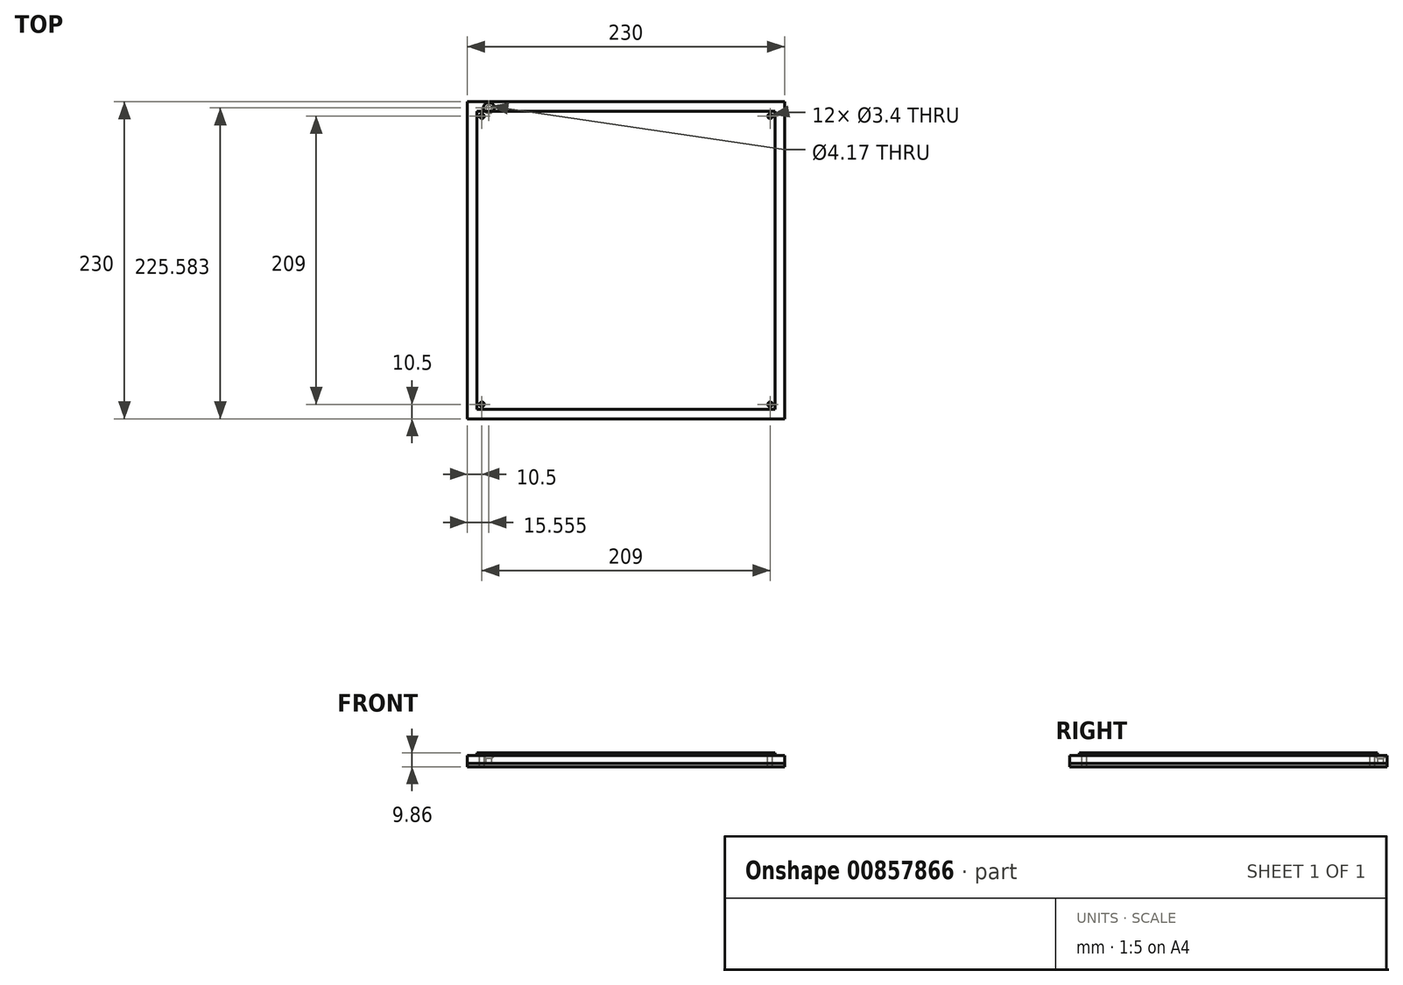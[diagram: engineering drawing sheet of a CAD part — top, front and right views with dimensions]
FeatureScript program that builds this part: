
annotation { "Feature Type Name" : "Feature", "Feature Type Description" : "" }
export const myFeature = defineFeature(function(context is Context, id is Id, definition is map)
    precondition{}
    {
        {
            var Q0;
            Q0=qCreatedBy(makeId("Top.planeOp"),FACE);
            var sketch = newSketch(context, id + "F0", { "sketchPlane" : qUnion([Q0])});
            skLineSegment(sketch, "E0.bottom", {"start": v(108, -108) * mm, "end": v(-108, -108) * mm});
            skLineSegment(sketch, "E0.top", {"start": v(108, 108) * mm, "end": v(-108, 108) * mm});
            skLineSegment(sketch, "E0.left", {"start": v(108, -108) * mm, "end": v(108, 108) * mm});
            skLineSegment(sketch, "E0.right", {"start": v(-108, -108) * mm, "end": v(-108, 108) * mm});
            skPoint(sketch, "E0.middle", {"position": v(0, 0) * mm});
            skCircle(sketch, "E1", {"center": v(-104.5, 104.5) * mm, "radius": 1.7 * mm});
            skCircle(sketch, "E2", {"center": v(104.5, 104.5) * mm, "radius": 1.7 * mm});
            skCircle(sketch, "E3", {"center": v(-104.5, -104.5) * mm, "radius": 1.7 * mm});
            skCircle(sketch, "E4", {"center": v(104.5, -104.5) * mm, "radius": 1.7 * mm});
            skSolve(sketch);
        }
        {
            var Q0;
            Q0 = qSketchRegion(id + "F0", true);
            extrude(context, id + "F1", {"entities" : qUnion([Q0]), "depth" : 1.86 * mm, "offsetDistance" : 25 * mm});
        }
        {
            var Q0;
            Q0=qCreatedBy(makeId("Top.planeOp"),FACE);
            var sketch = newSketch(context, id + "F2", { "sketchPlane" : qUnion([Q0])});
            skLineSegment(sketch, "E5.bottom", {"start": v(115, -115) * mm, "end": v(-115, -115) * mm});
            skLineSegment(sketch, "E5.top", {"start": v(115, 115) * mm, "end": v(-115, 115) * mm});
            skLineSegment(sketch, "E5.left", {"start": v(115, -115) * mm, "end": v(115, 115) * mm});
            skLineSegment(sketch, "E5.right", {"start": v(-115, -115) * mm, "end": v(-115, 115) * mm});
            skPoint(sketch, "E5.middle", {"position": v(0, 0) * mm});
            skCircle(sketch, "E6.0", {"center": v(-104.5, 104.5) * mm, "radius": 1.7 * mm});
            skCircle(sketch, "E7.0", {"center": v(104.5, 104.5) * mm, "radius": 1.7 * mm});
            skCircle(sketch, "E8.0", {"center": v(104.5, -104.5) * mm, "radius": 1.7 * mm});
            skCircle(sketch, "E9.0", {"center": v(-104.5, -104.5) * mm, "radius": 1.7 * mm});
            skLineSegment(sketch, "E10", {"start": v(-159.91, 110.58) * mm, "end": v(197.11, 110.58) * mm, "construction": true});
            skPoint(sketch, "E11", {"position": v(-99.44, 110.58) * mm});
            skSolve(sketch);
        }
        {
            var Q0;
            Q0 = qSketchRegion(id + "F2", true);
            extrude(context, id + "F3", {"entities" : qUnion([Q0]), "oppositeDirection" : true, "depth" : 8 * mm, "offsetDistance" : 25 * mm});
        }
        {
            var Q0;
            Q0=makeQuery(id+"F2.imprint","IMPRINT",FACE,{"disambiguationData":[TD([[makeQuery(id+"F2.imprint","IMPRINT",EDGE,{"derivedFrom":sQuery(id+"F2.wireOp",EDGE,"E5.bottom")}),-1.0]])]});
            var sketch = newSketch(context, id + "F4", { "sketchPlane" : qUnion([Q0])});
            skLineSegment(sketch, "E12.0.0", {"start": v(115, -115) * mm, "end": v(115, 115) * mm});
            skLineSegment(sketch, "E12.0.1", {"start": v(115, 115) * mm, "end": v(-115, 115) * mm});
            skLineSegment(sketch, "E12.0.2", {"start": v(-115, 115) * mm, "end": v(-115, -115) * mm});
            skLineSegment(sketch, "E12.0.3", {"start": v(-115, -115) * mm, "end": v(115, -115) * mm});
            skCircle(sketch, "E13.0", {"center": v(-104.5, 104.5) * mm, "radius": 1.7 * mm});
            skCircle(sketch, "E14.0", {"center": v(104.5, 104.5) * mm, "radius": 1.7 * mm});
            skCircle(sketch, "E15.0", {"center": v(104.5, -104.5) * mm, "radius": 1.7 * mm});
            skCircle(sketch, "E16.0", {"center": v(-104.5, -104.5) * mm, "radius": 1.7 * mm});
            skSolve(sketch);
        }
        {
            var Q0;
            Q0 = qSketchRegion(id + "F4", true);
            extrude(context, id + "F5", {"entities" : qUnion([Q0]), "oppositeDirection" : true, "depth" : 5.5 * mm, "offsetDistance" : 25 * mm});
        }
        {
            var Q0;
            Q0=sQuery(id+"F2.wireOp",VERTEX,"E11");
            var Q1;
            Q1=makeQuery(id+"F5.opExtrude","SWEPT_BODY",BODY,{"disambiguationData":[OSD([sQuery(id+"F4.wireOp",EDGE,"E12.0.0"),sQuery(id+"F4.wireOp",EDGE,"E12.0.1"),sQuery(id+"F4.wireOp",EDGE,"E12.0.2"),sQuery(id+"F4.wireOp",EDGE,"E12.0.3")])]});
            hole(context, id + "F6", {"style" : HoleStyle.C_SINK, "endStyle" : HoleEndStyle.THROUGH, "holeDiameter" : 4.17 * mm, "cSinkDiameter" : 7.92 * mm, "cSinkAngle" : 82 * degree, "majorDiameter" : 5 * mm, "isTappedThrough" : true, "tappedDepth" : 12 * mm, "tapClearance" : 3, "startFromSketch" : true, "locations" : qUnion([Q0]), "scope" : qUnion([Q1])});
        }
    });
